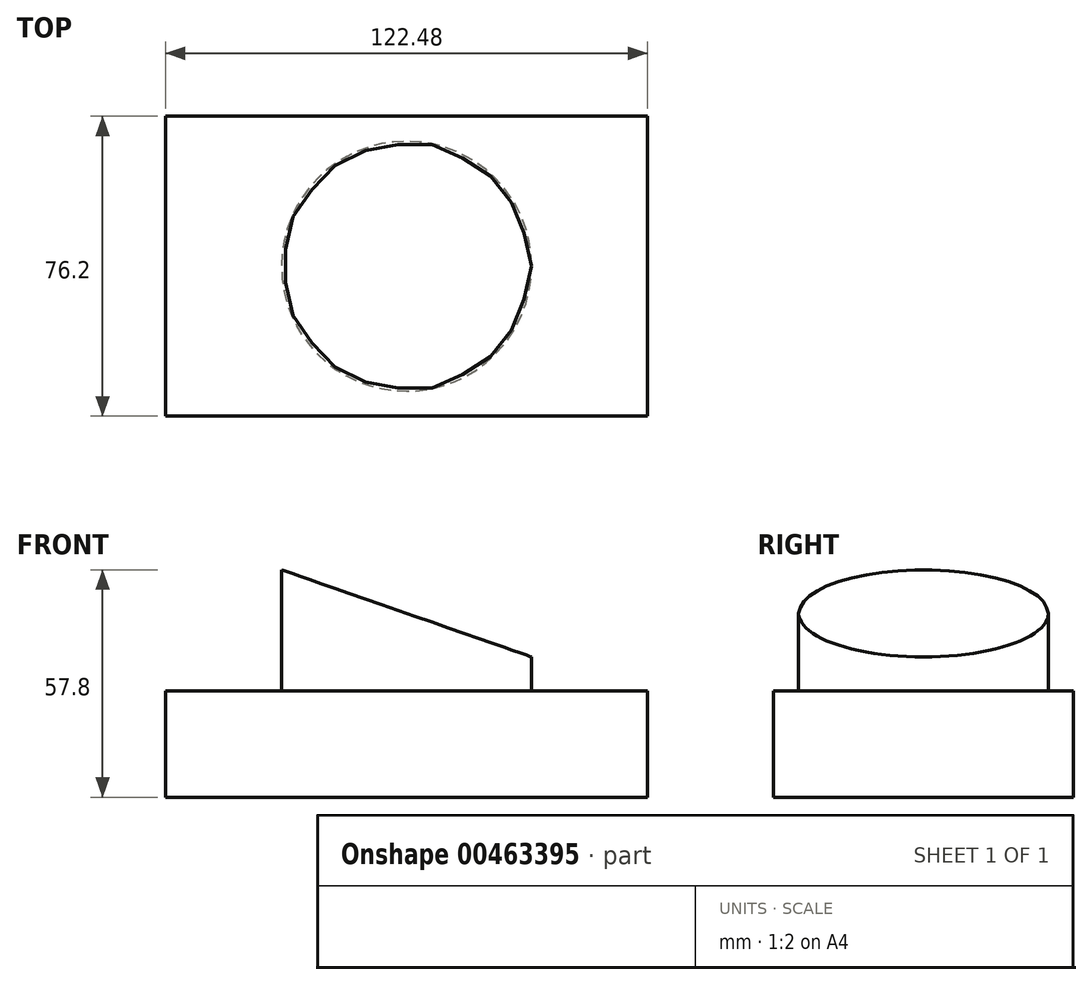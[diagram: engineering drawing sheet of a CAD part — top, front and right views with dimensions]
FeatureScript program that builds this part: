
annotation { "Feature Type Name" : "Feature", "Feature Type Description" : "" }
export const myFeature = defineFeature(function(context is Context, id is Id, definition is map)
    precondition{}
    {
        {
            var Q0;
            Q0=qCreatedBy(makeId("Front.planeOp"),FACE);
            var sketch = newSketch(context, id + "F0", { "sketchPlane" : qUnion([Q0])});
            skLineSegment(sketch, "E0.bottom", {"start": v(61.24, 13.48) * mm, "end": v(-61.24, 13.48) * mm});
            skLineSegment(sketch, "E0.top", {"start": v(61.24, -13.48) * mm, "end": v(-61.24, -13.48) * mm});
            skLineSegment(sketch, "E0.left", {"start": v(61.24, 13.48) * mm, "end": v(61.24, -13.48) * mm});
            skLineSegment(sketch, "E0.right", {"start": v(-61.24, 13.48) * mm, "end": v(-61.24, -13.48) * mm});
            skPoint(sketch, "E0.middle", {"position": v(0, 0) * mm});
            skSolve(sketch);
        }
        {
            var Q0;
            Q0=makeQuery(id+"F0.imprint","IMPRINT",FACE,{"disambiguationData":[TD([[makeQuery(id+"F0.imprint","IMPRINT",EDGE,{"derivedFrom":sQuery(id+"F0.wireOp",EDGE,"E0.bottom")}),1.0]])]});
            extrude(context, id + "F1", {"entities" : qUnion([Q0]), "depth" : 76.2 * mm});
        }
        {
            var Q0;
            Q0=makeQuery(id+"F1.opExtrude","SWEPT_FACE",FACE,{"disambiguationData":[OSD([sQuery(id+"F0.wireOp",EDGE,"E0.bottom")])]});
            var sketch = newSketch(context, id + "F2", { "sketchPlane" : qUnion([Q0])});
            skCircle(sketch, "E1", {"center": v(0, -38.1) * mm, "radius": 31.75 * mm});
            skPoint(sketch, "E2", {"position": v(0, -76.2) * mm});
            skSolve(sketch);
        }
        {
            var Q0;
            Q0=makeQuery(id+"F2.imprint","IMPRINT",FACE,{"disambiguationData":[TD([[makeQuery(id+"F2.imprint","IMPRINT",EDGE,{"derivedFrom":sQuery(id+"F2.wireOp",EDGE,"E1")}),1.0]])]});
            extrude(context, id + "F3", {"entities" : qUnion([Q0]), "operationType" : NewBodyOperationType.ADD, "depth" : 38.1 * mm});
        }
        {
            var Q0;
            Q0=qCreatedBy(makeId("Front.planeOp"),FACE);
            var sketch = newSketch(context, id + "F4", { "sketchPlane" : qUnion([Q0])});
            skLineSegment(sketch, "E3", {"start": v(-120.33, 75.2) * mm, "end": v(38.98, 19.65) * mm});
            skLineSegment(sketch, "E4", {"start": v(38.98, 19.65) * mm, "end": v(38.98, 69.25) * mm});
            skLineSegment(sketch, "E5", {"start": v(38.98, 69.25) * mm, "end": v(-120.33, 75.2) * mm});
            skSolve(sketch);
        }
        {
            var Q0;
            Q0=makeQuery(id+"F4.imprint","IMPRINT",FACE,{"disambiguationData":[TD([[makeQuery(id+"F4.imprint","IMPRINT",EDGE,{"derivedFrom":sQuery(id+"F4.wireOp",EDGE,"E3")}),1.0]])]});
            extrude(context, id + "F5", {"entities" : qUnion([Q0]), "operationType" : NewBodyOperationType.REMOVE, "depth" : 92.7 * mm});
        }
    });
